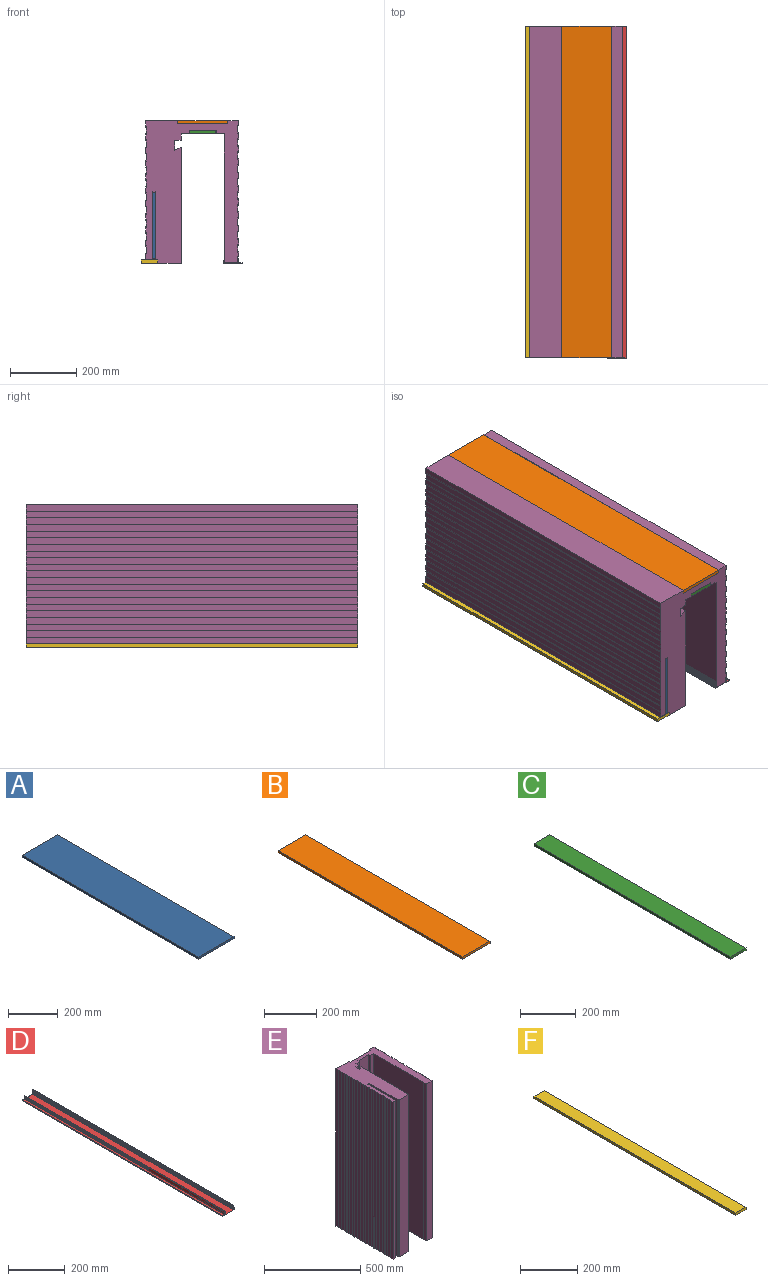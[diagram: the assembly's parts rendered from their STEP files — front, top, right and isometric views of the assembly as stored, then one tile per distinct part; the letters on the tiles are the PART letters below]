
ASSEMBLY  parts=6 mates=5
PART A: 6 faces, bbox 200x1000x10 mm
  f0: plane 1000x10mm, normal (-1,0,0), area 10000mm2, adj f1,f3,f4,f5
  f1: plane 1000x200mm, normal (0,0,-1), area 200000mm2, adj f0,f2,f4,f5
  f2: plane 1000x10mm, normal (1,0,0), area 10000mm2, adj f1,f3,f4,f5
  f3: plane 1000x200mm, normal (0,0,1), area 200000mm2, adj f0,f2,f4,f5
  f4: plane 200x10mm, normal (0,-1,0), area 2000mm2, adj f0,f1,f2,f3
  f5: plane 200x10mm, normal (0,1,0), area 2000mm2, adj f0,f1,f2,f3
PART B: 6 faces, bbox 150x1000x10 mm
  f0: plane 1000x10mm, normal (-1,0,0), area 10000mm2, adj f1,f3,f4,f5
  f1: plane 1000x150mm, normal (0,0,-1), area 150000mm2, adj f0,f2,f4,f5
  f2: plane 1000x10mm, normal (1,0,0), area 10000mm2, adj f1,f3,f4,f5
  f3: plane 1000x150mm, normal (0,0,1), area 150000mm2, adj f0,f2,f4,f5
  f4: plane 150x10mm, normal (0,-1,0), area 1500mm2, adj f0,f1,f2,f3
  f5: plane 150x10mm, normal (0,1,0), area 1500mm2, adj f0,f1,f2,f3
PART C: 6 faces, bbox 80x1000x10 mm
  f0: plane 1000x10mm, normal (-1,0,0), area 10000mm2, adj f1,f3,f4,f5
  f1: plane 1000x80mm, normal (0,0,-1), area 80000mm2, adj f0,f2,f4,f5
  f2: plane 1000x10mm, normal (1,0,0), area 10000mm2, adj f1,f3,f4,f5
  f3: plane 1000x80mm, normal (0,0,1), area 80000mm2, adj f0,f2,f4,f5
  f4: plane 80x10mm, normal (0,-1,0), area 800mm2, adj f0,f1,f2,f3
  f5: plane 80x10mm, normal (0,1,0), area 800mm2, adj f0,f1,f2,f3
PART D: 62 faces, bbox 57.5x1000x21 mm
  f0: plane 1000x14.3mm, normal (-1,0,0), area 14303.9mm2, adj f1,f2,f60,f61
  f1: plane 57.5x21mm, normal (0,-1,0), area 145.8mm2, adj f0,f2,f3,f4,f5,f6,f7,f8
  f2: plane 1000x11mm, normal (0,0,1), area 11000mm2, adj f0,f1,f3,f60
  f3: plane 1000x1.5mm, normal (1,0,0), area 1500mm2, adj f1,f2,f4,f60
  f4: plane 1000x1.5mm, normal (0,0,1), area 1500mm2, adj f1,f3,f5,f60
  f5: plane 1000x3mm, normal (-1,0,0), area 3000mm2, adj f1,f4,f6,f60
  f6: plane 1000x57.5mm, normal (0,0,-1), area 57500mm2, adj f1,f5,f7,f60
  f7: plane 1000x4mm, normal (1,0,0), area 4000mm2, adj f1,f6,f8,f60
  f8: plane 1000x1mm, normal (0,0,1), area 1000mm2, adj f1,f7,f9,f60
  f9: plane 1000x3mm, normal (-1,0,0), area 3000mm2, adj f1,f8,f10,f60
  f10: plane 1000x1mm, normal (0,0,1), area 1000mm2, adj f1,f9,f11,f60
  f11: plane 1000x7mm, normal (1,0,0), area 7000mm2, adj f1,f10,f12,f60
  f12: plane 1000x1mm, normal (0,0,-1), area 1000mm2, adj f1,f11,f13,f60
  f13: plane 1000x3mm, normal (-1,0,0), area 3000mm2, adj f1,f12,f14,f60
  f14: plane 1000x1mm, normal (0,0,-1), area 1000mm2, adj f1,f13,f15,f60
  f15: plane 1000x4mm, normal (1,0,0), area 4000mm2, adj f1,f14,f16,f60
  f16: plane 1000x2mm, normal (0,0,1), area 2000mm2, adj f1,f15,f17,f60
  f17: plane 1000x12mm, normal (1,0,0), area 12000mm2, adj f1,f16,f18,f60
  f18: plane 1000x1mm, normal (0,0,1), area 1000mm2, adj f1,f17,f19,f60
  f19: plane 1000x1.73mm, normal (-0.87,0,0.5), area 2000mm2, adj f1,f18,f20,f60
  f20: plane 1000x1mm, normal (0,0,-1), area 1000mm2, adj f1,f19,f21,f60
  f21: plane 1000x1.73mm, normal (-0.87,0,0.5), area 2000mm2, adj f1,f20,f22,f60
  f22: plane 1000x1mm, normal (0,0,-1), area 1000mm2, adj f1,f21,f23,f60
  f23: plane 1000x1.73mm, normal (-0.87,0,0.5), area 2000mm2, adj f1,f22,f24,f60
  f24: plane 1000x1mm, normal (0,0,-1), area 1000mm2, adj f1,f23,f25,f60
  f25: plane 1000x1.73mm, normal (-0.87,0,0.5), area 2000mm2, adj f1,f24,f26,f60
  f26: plane 1000x1mm, normal (0,0,-1), area 1000mm2, adj f1,f25,f27,f60
  f27: plane 1000x1.73mm, normal (-0.87,0,0.5), area 2000mm2, adj f1,f26,f28,f60
  f28: plane 1000x1mm, normal (0,0,-1), area 1000mm2, adj f1,f27,f29,f60
  f29: plane 1000x1.73mm, normal (-0.87,0,0.5), area 2000mm2, adj f1,f28,f30,f60
  f30: plane 1000x1mm, normal (0,0,-1), area 1000mm2, adj f1,f29,f31,f60
  f31: plane 1000x1.73mm, normal (-0.87,0,0.5), area 2000mm2, adj f1,f30,f32,f60
  f32: plane 1000x1mm, normal (0,0,-1), area 1000mm2, adj f1,f31,f33,f60
  f33: plane 1000x1.73mm, normal (-0.87,0,0.5), area 2000mm2, adj f1,f32,f34,f60
  f34: plane 1000x1mm, normal (0,0,-1), area 1000mm2, adj f1,f33,f35,f60
  f35: plane 1000x1.73mm, normal (-0.87,0,0.5), area 2000mm2, adj f1,f34,f36,f60
  f36: plane 1000x1mm, normal (0,0,-1), area 1000mm2, adj f1,f35,f37,f60
  f37: plane 1000x1.73mm, normal (-0.87,0,0.5), area 2000mm2, adj f1,f36,f38,f60
  f38: plane 1000x1mm, normal (0,0,-1), area 1000mm2, adj f1,f37,f39,f60
  f39: plane 1000x1.73mm, normal (-0.87,0,0.5), area 2000mm2, adj f1,f38,f40,f60
  f40: plane 1000x1mm, normal (0,0,-1), area 1000mm2, adj f1,f39,f41,f60
  f41: plane 1000x0.45mm, normal (-1,0,0), area 447.4mm2, adj f1,f40,f42,f60
  f42: plane 1000x41mm, normal (0,0,1), area 41000mm2, adj f1,f41,f43,f60
  f43: plane 1000x0.45mm, normal (1,0,0), area 447.4mm2, adj f1,f42,f44,f60
  f44: plane 1000x1mm, normal (0,0,-1), area 1000mm2, adj f1,f43,f45,f60
  f45: plane 1000x1.73mm, normal (0.87,0,0.5), area 2000mm2, adj f1,f44,f46,f60
  f46: plane 1000x1mm, normal (0,0,-1), area 1000mm2, adj f1,f45,f47,f60
  f47: plane 1000x1.73mm, normal (0.87,0,0.5), area 2000mm2, adj f1,f46,f48,f60
  f48: plane 1000x1mm, normal (0,0,-1), area 1000mm2, adj f1,f47,f49,f60
  f49: plane 1000x1.73mm, normal (0.87,0,0.5), area 2000mm2, adj f1,f48,f50,f60
  f50: plane 1000x1mm, normal (0,0,-1), area 1000mm2, adj f1,f49,f51,f60
  f51: plane 1000x1.73mm, normal (0.87,0,0.5), area 2000mm2, adj f1,f50,f52,f60
  f52: plane 1000x1mm, normal (0,0,-1), area 1000mm2, adj f1,f51,f53,f60
  f53: plane 1000x1.73mm, normal (0.87,0,0.5), area 2000mm2, adj f1,f52,f54,f60
  f54: plane 1000x1mm, normal (0,0,-1), area 1000mm2, adj f1,f53,f55,f60
  f55: plane 1000x1.73mm, normal (0.87,0,0.5), area 2000mm2, adj f1,f54,f56,f60
  f56: plane 1000x1mm, normal (0,0,-1), area 1000mm2, adj f1,f55,f57,f60
  f57: plane 1000x1.73mm, normal (0.87,0,0.5), area 2000mm2, adj f1,f56,f58,f60
  f58: plane 1000x1mm, normal (0,0,-1), area 1000mm2, adj f1,f57,f59,f60
  f59: plane 1000x1.73mm, normal (0.87,0,0.5), area 2000mm2, adj f1,f58,f60,f61
  f60: plane 57.5x21mm, normal (0,1,0), area 145.8mm2, adj f0,f2,f3,f4,f5,f6,f7,f8
  f61: plane 1000x1mm, normal (0,0,1), area 1000mm2, adj f0,f1,f59,f60
PART E: 112 faces, bbox 280x430x1000 mm
  f0: plane 1000x20mm, normal (-1,0,0), area 20000mm2, adj f50,f51,f106,f110
  f1: plane 1000x20mm, normal (-1,0,0), area 20000mm2, adj f50,f51,f103,f107
  f2: plane 1000x20mm, normal (-1,0,0), area 20000mm2, adj f50,f51,f100,f104
  f3: plane 1000x20mm, normal (-1,0,0), area 20000mm2, adj f50,f51,f97,f101
  f4: plane 1000x20mm, normal (-1,0,0), area 20000mm2, adj f50,f51,f94,f98
  f5: plane 1000x20mm, normal (-1,0,0), area 20000mm2, adj f50,f51,f91,f95
  f6: plane 1000x20mm, normal (-1,0,0), area 20000mm2, adj f50,f51,f88,f92
  f7: plane 1000x20mm, normal (-1,0,0), area 20000mm2, adj f50,f51,f85,f89
  f8: plane 1000x20mm, normal (-1,0,0), area 20000mm2, adj f50,f51,f82,f86
  f9: plane 1000x20mm, normal (-1,0,0), area 20000mm2, adj f21,f50,f51,f83
  f10: plane 1000x15mm, normal (1,0,0), area 15000mm2, adj f45,f50,f51,f79
  f11: plane 1000x20mm, normal (1,0,0), area 20000mm2, adj f50,f51,f76,f80
  f12: plane 1000x20mm, normal (1,0,0), area 20000mm2, adj f50,f51,f73,f77
  f13: plane 1000x20mm, normal (1,0,0), area 20000mm2, adj f50,f51,f70,f74
  f14: plane 1000x20mm, normal (1,0,0), area 20000mm2, adj f50,f51,f67,f71
  f15: plane 1000x20mm, normal (1,0,0), area 20000mm2, adj f50,f51,f64,f68
  f16: plane 1000x20mm, normal (1,0,0), area 20000mm2, adj f50,f51,f61,f65
  f17: plane 1000x20mm, normal (1,0,0), area 20000mm2, adj f50,f51,f58,f62
  f18: plane 1000x20mm, normal (1,0,0), area 20000mm2, adj f50,f51,f55,f59
  f19: plane 1000x20mm, normal (1,0,0), area 20000mm2, adj f50,f51,f52,f56
  f20: plane 1000x10mm, normal (1,0,0), area 10000mm2, adj f21,f49,f50,f51
  f21: plane 1000x96.75mm, normal (0,1,0), area 96750mm2, adj f9,f20,f50,f51
  f22: plane 1000x20mm, normal (-1,0,0), area 20000mm2, adj f23,f50,f51,f109
  f23: plane 1000x20.5mm, normal (0,-1,0), area 20500mm2, adj f22,f24,f50,f51
  f24: plane 1000x205mm, normal (1,0,0), area 205000mm2, adj f23,f25,f50,f51
  f25: cylinder r=10mm len=1000mm, axis (0,0,-1), area 11054.3mm2, adj f24,f26,f50,f51
  f26: plane 1000x205mm, normal (-1,0,0), area 205000mm2, adj f25,f27,f50,f51
  f27: plane 1000x6mm, normal (0,-1,0), area 6000mm2, adj f26,f28,f50,f51
  f28: plane 1000x10mm, normal (-1,0,0), area 10000mm2, adj f27,f29,f50,f51
  f29: plane 1000x70mm, normal (0,-1,0), area 70000mm2, adj f28,f30,f50,f51
  f30: plane 1000x350.19mm, normal (1,0,0), area 350190.5mm2, adj f29,f31,f50,f51
  f31: plane 1000x20mm, normal (-0.45,0.89,0), area 22446.5mm2, adj f30,f32,f50,f51
  f32: plane 1000x30mm, normal (1,0,0), area 30000mm2, adj f31,f33,f50,f51
  f33: plane 1000x20mm, normal (0,-1,0), area 20000mm2, adj f32,f34,f50,f51
  f34: plane 1000x20mm, normal (1,0,0), area 20000mm2, adj f33,f35,f50,f51
  f35: plane 1000x24.75mm, normal (0,-1,0), area 24750mm2, adj f34,f36,f50,f51
  f36: plane 1000x10mm, normal (1,0,0), area 10000mm2, adj f35,f37,f50,f51
  f37: plane 1000x80.5mm, normal (0,-1,0), area 80500mm2, adj f36,f38,f50,f51
  f38: plane 1000x10mm, normal (-1,0,0), area 10000mm2, adj f37,f39,f50,f51
  f39: plane 1000x24.75mm, normal (0,-1,0), area 24750mm2, adj f38,f40,f50,f51
  f40: plane 1000x367.5mm, normal (-1,0,0), area 367500mm2, adj f39,f41,f50,f51
  f41: plane 1000x2mm, normal (0,-1,0), area 2000mm2, adj f40,f42,f50,f51
  f42: plane 1000x21.5mm, normal (-1,0,0), area 21500mm2, adj f41,f43,f50,f51
  f43: plane 1000x39.1mm, normal (0,-1,0), area 39100mm2, adj f42,f44,f50,f51
  f44: plane 1000x18.5mm, normal (1,0,0), area 18500mm2, adj f43,f45,f50,f51
  f45: plane 1000x1.9mm, normal (0,-1,0), area 1900mm2, adj f10,f44,f50,f51
  f46: plane 1000x15.5mm, normal (1,0,0), area 15500mm2, adj f47,f50,f51,f53
  f47: plane 1000x32.75mm, normal (0,1,0), area 32750mm2, adj f46,f48,f50,f51
  f48: plane 1000x10mm, normal (-1,0,0), area 10000mm2, adj f47,f49,f50,f51
  f49: plane 1000x150.5mm, normal (0,1,0), area 150500mm2, adj f20,f48,f50,f51
  f50: plane 430x280mm, normal (0,0,1), area 63378.8mm2, adj f0,f1,f2,f3,f4,f5,f6,f7
  f51: plane 430x280mm, normal (0,0,-1), area 63378.8mm2, adj f0,f1,f2,f3,f4,f5,f6,f7
  f52: plane 1000x2mm, normal (-0.71,0.71,0), area 2828.4mm2, adj f19,f50,f51,f54
  f53: plane 1000x2mm, normal (-0.71,-0.71,0), area 2828.4mm2, adj f46,f50,f51,f54
  f54: plane 1000x24mm, normal (1,0,0), area 24000mm2, adj f50,f51,f52,f53
  f55: plane 1000x2mm, normal (-0.71,0.71,0), area 2828.4mm2, adj f18,f50,f51,f57
  f56: plane 1000x2mm, normal (-0.71,-0.71,0), area 2828.4mm2, adj f19,f50,f51,f57
  f57: plane 1000x24mm, normal (1,0,0), area 24000mm2, adj f50,f51,f55,f56
  f58: plane 1000x2mm, normal (-0.71,0.71,0), area 2828.4mm2, adj f17,f50,f51,f60
  f59: plane 1000x2mm, normal (-0.71,-0.71,0), area 2828.4mm2, adj f18,f50,f51,f60
  f60: plane 1000x24mm, normal (1,0,0), area 24000mm2, adj f50,f51,f58,f59
  f61: plane 1000x2mm, normal (-0.71,0.71,0), area 2828.4mm2, adj f16,f50,f51,f63
  f62: plane 1000x2mm, normal (-0.71,-0.71,0), area 2828.4mm2, adj f17,f50,f51,f63
  f63: plane 1000x24mm, normal (1,0,0), area 24000mm2, adj f50,f51,f61,f62
  f64: plane 1000x2mm, normal (-0.71,0.71,0), area 2828.4mm2, adj f15,f50,f51,f66
  f65: plane 1000x2mm, normal (-0.71,-0.71,0), area 2828.4mm2, adj f16,f50,f51,f66
  f66: plane 1000x24mm, normal (1,0,0), area 24000mm2, adj f50,f51,f64,f65
  f67: plane 1000x2mm, normal (-0.71,0.71,0), area 2828.4mm2, adj f14,f50,f51,f69
  f68: plane 1000x2mm, normal (-0.71,-0.71,0), area 2828.4mm2, adj f15,f50,f51,f69
  f69: plane 1000x24mm, normal (1,0,0), area 24000mm2, adj f50,f51,f67,f68
  f70: plane 1000x2mm, normal (-0.71,0.71,0), area 2828.4mm2, adj f13,f50,f51,f72
  f71: plane 1000x2mm, normal (-0.71,-0.71,0), area 2828.4mm2, adj f14,f50,f51,f72
  f72: plane 1000x24mm, normal (1,0,0), area 24000mm2, adj f50,f51,f70,f71
  f73: plane 1000x2mm, normal (-0.71,0.71,0), area 2828.4mm2, adj f12,f50,f51,f75
  f74: plane 1000x2mm, normal (-0.71,-0.71,0), area 2828.4mm2, adj f13,f50,f51,f75
  f75: plane 1000x24mm, normal (1,0,0), area 24000mm2, adj f50,f51,f73,f74
  f76: plane 1000x2mm, normal (-0.71,0.71,0), area 2828.4mm2, adj f11,f50,f51,f78
  f77: plane 1000x2mm, normal (-0.71,-0.71,0), area 2828.4mm2, adj f12,f50,f51,f78
  f78: plane 1000x24mm, normal (1,0,0), area 24000mm2, adj f50,f51,f76,f77
  f79: plane 1000x2mm, normal (-0.71,0.71,0), area 2828.4mm2, adj f10,f50,f51,f81
  f80: plane 1000x2mm, normal (-0.71,-0.71,0), area 2828.4mm2, adj f11,f50,f51,f81
  f81: plane 1000x24mm, normal (1,0,0), area 24000mm2, adj f50,f51,f79,f80
  f82: plane 1000x2mm, normal (0.71,0.71,0), area 2828.4mm2, adj f8,f50,f51,f84
  f83: plane 1000x2mm, normal (0.71,-0.71,0), area 2828.4mm2, adj f9,f50,f51,f84
  f84: plane 1000x24mm, normal (-1,0,0), area 24000mm2, adj f50,f51,f82,f83
  f85: plane 1000x2mm, normal (0.71,0.71,0), area 2828.4mm2, adj f7,f50,f51,f87
  f86: plane 1000x2mm, normal (0.71,-0.71,0), area 2828.4mm2, adj f8,f50,f51,f87
  f87: plane 1000x24mm, normal (-1,0,0), area 24000mm2, adj f50,f51,f85,f86
  f88: plane 1000x2mm, normal (0.71,0.71,0), area 2828.4mm2, adj f6,f50,f51,f90
  f89: plane 1000x2mm, normal (0.71,-0.71,0), area 2828.4mm2, adj f7,f50,f51,f90
  f90: plane 1000x24mm, normal (-1,0,0), area 24000mm2, adj f50,f51,f88,f89
  f91: plane 1000x2mm, normal (0.71,0.71,0), area 2828.4mm2, adj f5,f50,f51,f93
  f92: plane 1000x2mm, normal (0.71,-0.71,0), area 2828.4mm2, adj f6,f50,f51,f93
  f93: plane 1000x24mm, normal (-1,0,0), area 24000mm2, adj f50,f51,f91,f92
  f94: plane 1000x2mm, normal (0.71,0.71,0), area 2828.4mm2, adj f4,f50,f51,f96
  f95: plane 1000x2mm, normal (0.71,-0.71,0), area 2828.4mm2, adj f5,f50,f51,f96
  f96: plane 1000x24mm, normal (-1,0,0), area 24000mm2, adj f50,f51,f94,f95
  f97: plane 1000x2mm, normal (0.71,0.71,0), area 2828.4mm2, adj f3,f50,f51,f99
  f98: plane 1000x2mm, normal (0.71,-0.71,0), area 2828.4mm2, adj f4,f50,f51,f99
  f99: plane 1000x24mm, normal (-1,0,0), area 24000mm2, adj f50,f51,f97,f98
  f100: plane 1000x2mm, normal (0.71,0.71,0), area 2828.4mm2, adj f2,f50,f51,f102
  f101: plane 1000x2mm, normal (0.71,-0.71,0), area 2828.4mm2, adj f3,f50,f51,f102
  f102: plane 1000x24mm, normal (-1,0,0), area 24000mm2, adj f50,f51,f100,f101
  f103: plane 1000x2mm, normal (0.71,0.71,0), area 2828.4mm2, adj f1,f50,f51,f105
  f104: plane 1000x2mm, normal (0.71,-0.71,0), area 2828.4mm2, adj f2,f50,f51,f105
  f105: plane 1000x24mm, normal (-1,0,0), area 24000mm2, adj f50,f51,f103,f104
  f106: plane 1000x2mm, normal (0.71,0.71,0), area 2828.4mm2, adj f0,f50,f51,f108
  f107: plane 1000x2mm, normal (0.71,-0.71,0), area 2828.4mm2, adj f1,f50,f51,f108
  f108: plane 1000x24mm, normal (-1,0,0), area 24000mm2, adj f50,f51,f106,f107
  f109: plane 1000x2mm, normal (0.71,0.71,0), area 2828.4mm2, adj f22,f50,f51,f111
  f110: plane 1000x2mm, normal (0.71,-0.71,0), area 2828.4mm2, adj f0,f50,f51,f111
  f111: plane 1000x24mm, normal (-1,0,0), area 24000mm2, adj f50,f51,f109,f110
PART F: 6 faces, bbox 50x1000x10 mm
  f0: plane 1000x10mm, normal (-1,0,0), area 10000mm2, adj f1,f3,f4,f5
  f1: plane 1000x50mm, normal (0,0,-1), area 50000mm2, adj f0,f2,f4,f5
  f2: plane 1000x10mm, normal (1,0,0), area 10000mm2, adj f1,f3,f4,f5
  f3: plane 1000x50mm, normal (0,0,1), area 50000mm2, adj f0,f2,f4,f5
  f4: plane 50x10mm, normal (0,-1,0), area 500mm2, adj f0,f1,f2,f3
  f5: plane 50x10mm, normal (0,1,0), area 500mm2, adj f0,f1,f2,f3
PLACE A rot(axis=(0,1,0),90deg) t=(-266.83,500,-151.72)mm
PLACE B t=(-190.83,500,55.28)mm fixed
PLACE C t=(-155.83,500,25.28)mm
PLACE D rot(axis=(0,0,1),180deg) t=(-52.58,-500,-365.22)mm
PLACE E rot(axis=(1,0,0),90deg) t=(-169.11,500,-107.78)mm
PLACE F t=(-300.58,500,-364.72)mm
MATE fastened A.f4 <-> E.f50  axis (0,-1,0) through (-256.58,-500,-149.72)mm
MATE fastened E.f50 <-> B.f4  axis (0,-1,0) through (-190.83,-500,65.28)mm
MATE fastened C.f4 <-> E.f50  axis (0,-1,0) through (-155.83,-500,35.28)mm
MATE fastened D.f60 <-> E.f50  axis (0,-1,0) through (-48.58,-500,-363.72)mm
MATE fastened F.f4 <-> E.f50  axis (0,-1,0) through (-250.58,-500,-354.72)mm
